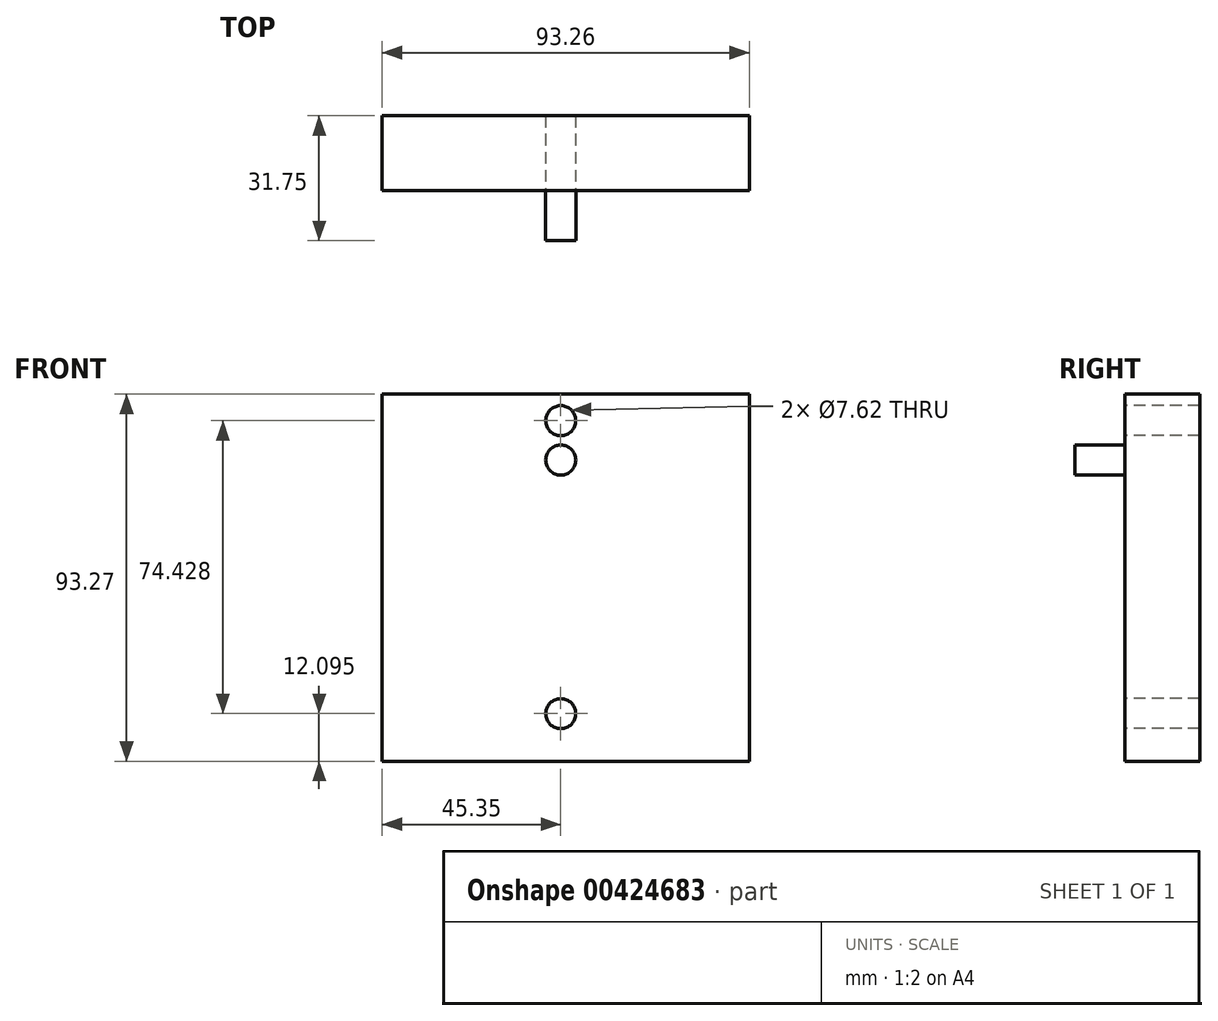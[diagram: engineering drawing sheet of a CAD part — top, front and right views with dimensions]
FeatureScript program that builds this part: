
annotation { "Feature Type Name" : "Feature", "Feature Type Description" : "" }
export const myFeature = defineFeature(function(context is Context, id is Id, definition is map)
    precondition{}
    {
        {
            var Q0;
            Q0=qCreatedBy(makeId("Front.planeOp"),FACE);
            var sketch = newSketch(context, id + "F0", { "sketchPlane" : qUnion([Q0])});
            skLineSegment(sketch, "E0", {"start": v(-45.35, 55.59) * mm, "end": v(-45.35, -37.68) * mm});
            skLineSegment(sketch, "E1", {"start": v(-45.35, -37.68) * mm, "end": v(47.91, -37.68) * mm});
            skLineSegment(sketch, "E2", {"start": v(47.91, -37.68) * mm, "end": v(47.91, 55.59) * mm});
            skLineSegment(sketch, "E3", {"start": v(47.91, 55.59) * mm, "end": v(-45.35, 55.59) * mm});
            skSolve(sketch);
        }
        {
            var Q0;
            Q0=makeQuery(id+"F0.imprint","IMPRINT",FACE,{"disambiguationData":[TD([[makeQuery(id+"F0.imprint","IMPRINT",EDGE,{"derivedFrom":sQuery(id+"F0.wireOp",EDGE,"E0")}),1.0]])]});
            extrude(context, id + "F1", {"entities" : qUnion([Q0]), "depth" : 19.05 * mm});
        }
        {
            var Q0;
            Q0=makeQuery(id+"F1.opExtrude","CAP_FACE",FACE,{"disambiguationData":[OSD([sQuery(id+"F0.wireOp",EDGE,"E0"),sQuery(id+"F0.wireOp",EDGE,"E1"),sQuery(id+"F0.wireOp",EDGE,"E2"),sQuery(id+"F0.wireOp",EDGE,"E3")])],"isStart":false});
            var sketch = newSketch(context, id + "F2", { "sketchPlane" : qUnion([Q0])});
            skCircle(sketch, "E4", {"center": v(0, 38.84) * mm, "radius": 3.81 * mm});
            skSolve(sketch);
        }
        {
            var Q0;
            Q0=makeQuery(id+"F2.imprint","IMPRINT",FACE,{"disambiguationData":[TD([[makeQuery(id+"F2.imprint","IMPRINT",EDGE,{"derivedFrom":sQuery(id+"F2.wireOp",EDGE,"E4")}),1.0]])]});
            extrude(context, id + "F3", {"entities" : qUnion([Q0]), "operationType" : NewBodyOperationType.ADD, "depth" : 12.7 * mm});
        }
        {
            var Q0;
            Q0=makeQuery(id+"F1.opExtrude","CAP_FACE",FACE,{"disambiguationData":[OSD([sQuery(id+"F0.wireOp",EDGE,"E0"),sQuery(id+"F0.wireOp",EDGE,"E1"),sQuery(id+"F0.wireOp",EDGE,"E2"),sQuery(id+"F0.wireOp",EDGE,"E3")])],"isStart":false});
            var sketch = newSketch(context, id + "F4", { "sketchPlane" : qUnion([Q0])});
            skCircle(sketch, "E5", {"center": v(0, 48.84) * mm, "radius": 4.6 * mm});
            skCircle(sketch, "E6", {"center": v(0, -25.58) * mm, "radius": 4.93 * mm});
            skSolve(sketch);
        }
        {
            var Q0;
            Q0=sQuery(id+"F4.wireOp",VERTEX,"E5.center");
            var Q1;
            Q1=sQuery(id+"F4.wireOp",VERTEX,"E6.center");
            var Q2;
            Q2=makeQuery(id+"F1.opExtrude","SWEPT_BODY",BODY,{"disambiguationData":[OSD([sQuery(id+"F0.wireOp",EDGE,"E0"),sQuery(id+"F0.wireOp",EDGE,"E1"),sQuery(id+"F0.wireOp",EDGE,"E2"),sQuery(id+"F0.wireOp",EDGE,"E3")])]});
            hole(context, id + "F5", {"style" : HoleStyle.SIMPLE, "endStyle" : HoleEndStyle.THROUGH, "holeDiameter" : 7.62 * mm, "isTappedThrough" : true, "tappedDepth" : 12.7 * mm, "tapClearance" : 3, "locations" : qUnion([Q0, Q1]), "scope" : qUnion([Q2])});
        }
    });
